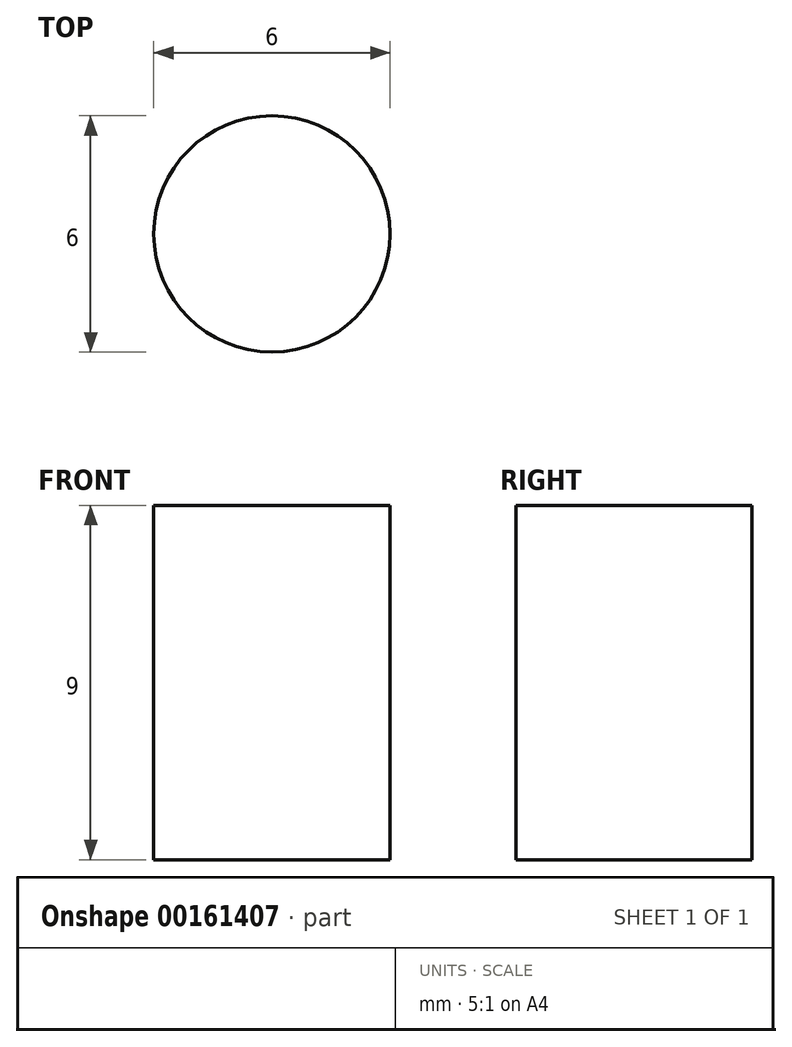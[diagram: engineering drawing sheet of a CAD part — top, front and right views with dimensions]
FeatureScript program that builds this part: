
annotation { "Feature Type Name" : "Feature", "Feature Type Description" : "" }
export const myFeature = defineFeature(function(context is Context, id is Id, definition is map)
    precondition{}
    {
        {
            var Q0;
            Q0=qCreatedBy(makeId("Top.planeOp"),FACE);
            var sketch = newSketch(context, id + "F0", { "sketchPlane" : qUnion([Q0])});
            skCircle(sketch, "E0", {"center": v(0, 0) * mm, "radius": 3 * mm});
            skSolve(sketch);
        }
        {
            var Q0;
            Q0=qSketchRegion(id+"F0",true);
            extrude(context, id + "F1", {"entities" : qUnion([Q0]), "oppositeDirection" : true, "depth" : 9 * mm});
        }
    });
